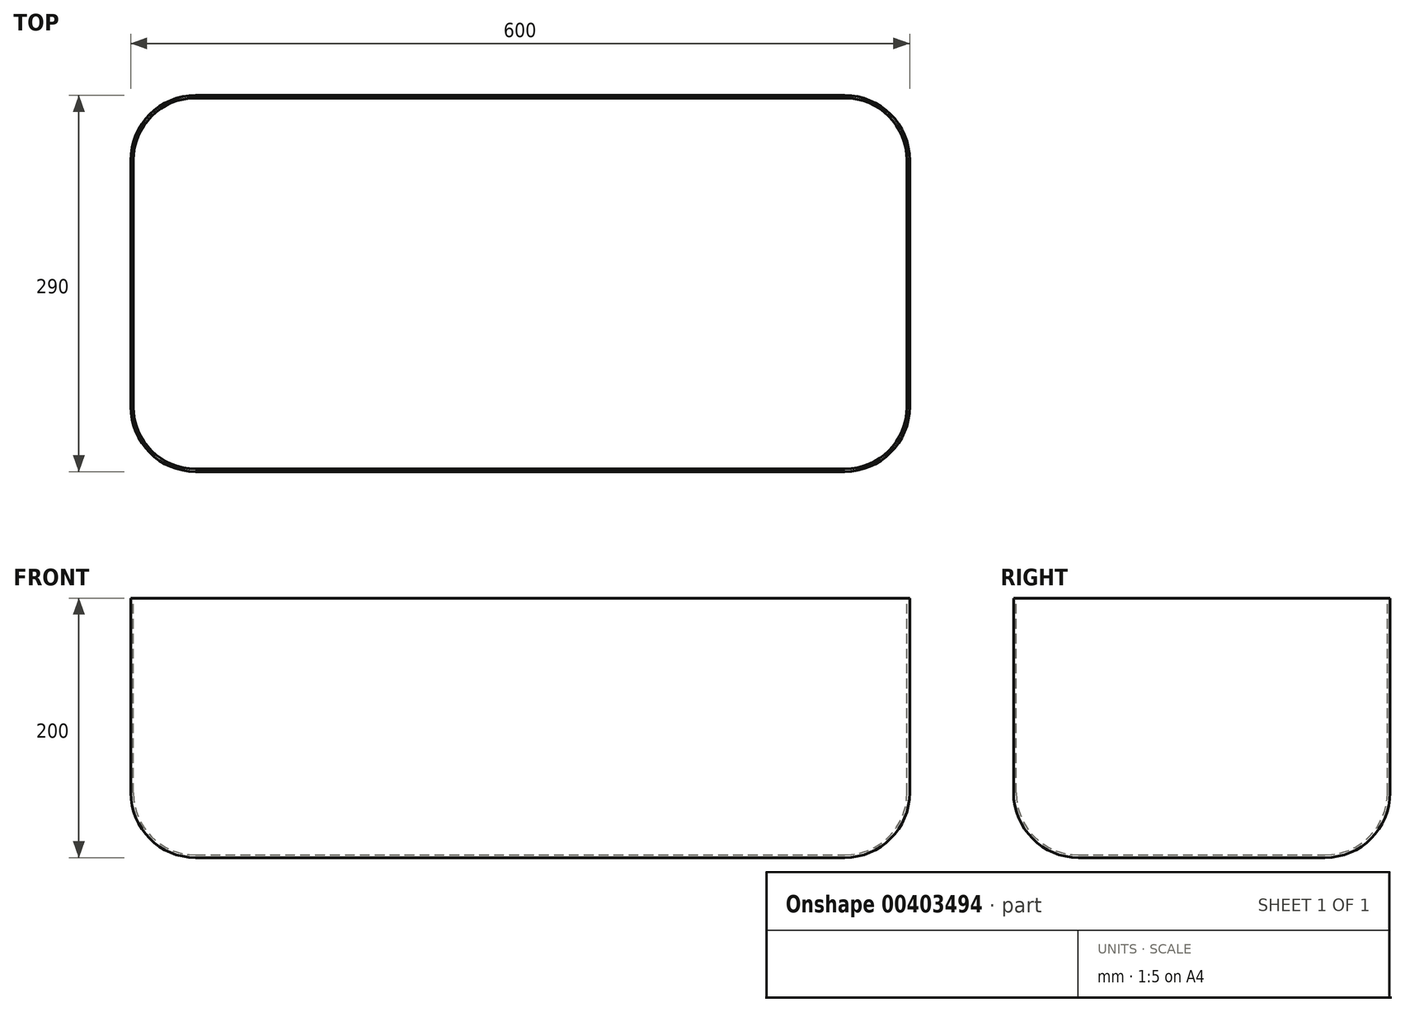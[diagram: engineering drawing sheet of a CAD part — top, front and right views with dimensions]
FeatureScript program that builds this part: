
annotation { "Feature Type Name" : "Feature", "Feature Type Description" : "" }
export const myFeature = defineFeature(function(context is Context, id is Id, definition is map)
    precondition{}
    {
        {
            var Q0;
            Q0=qCreatedBy(makeId("Front.planeOp"),FACE);
            var sketch = newSketch(context, id + "F0", { "sketchPlane" : qUnion([Q0])});
            skLineSegment(sketch, "E0.bottom", {"start": v(0, 0) * mm, "end": v(600, 0) * mm});
            skLineSegment(sketch, "E0.top", {"start": v(0, 200) * mm, "end": v(600, 200) * mm});
            skLineSegment(sketch, "E0.left", {"start": v(0, 0) * mm, "end": v(0, 200) * mm});
            skLineSegment(sketch, "E0.right", {"start": v(600, 0) * mm, "end": v(600, 200) * mm});
            skSolve(sketch);
        }
        {
            var Q0;
            Q0=qSketchRegion(id+"F0",true);
            extrude(context, id + "F1", {"entities" : qUnion([Q0]), "depth" : 290 * mm});
        }
        {
            var Q0;
            Q0=makeQuery(id+"F1.opExtrude","CAP_EDGE",EDGE,{"disambiguationData":[OSD([sQuery(id+"F0.wireOp",EDGE,"E0.right")])],"isStart":false});
            var Q1;
            Q1=makeQuery(id+"F1.opExtrude","CAP_EDGE",EDGE,{"disambiguationData":[OSD([sQuery(id+"F0.wireOp",EDGE,"E0.left")])],"isStart":false});
            var Q2;
            Q2=makeQuery(id+"F1.opExtrude","CAP_EDGE",EDGE,{"disambiguationData":[OSD([sQuery(id+"F0.wireOp",EDGE,"E0.right")])],"isStart":true});
            var Q3;
            Q3=makeQuery(id+"F1.opExtrude","SWEPT_EDGE",EDGE,{"disambiguationData":[OSD([sQuery(id+"F0.wireOp",EDGE,"E0.bottom"),sQuery(id+"F0.wireOp",EDGE,"E0.right")])]});
            var Q4;
            Q4=makeQuery(id+"F1.opExtrude","CAP_EDGE",EDGE,{"disambiguationData":[OSD([sQuery(id+"F0.wireOp",EDGE,"E0.bottom")])],"isStart":false});
            var Q5;
            Q5=makeQuery(id+"F1.opExtrude","SWEPT_EDGE",EDGE,{"disambiguationData":[OSD([sQuery(id+"F0.wireOp",EDGE,"E0.bottom"),sQuery(id+"F0.wireOp",EDGE,"E0.left")])]});
            var Q6;
            Q6=makeQuery(id+"F1.opExtrude","CAP_EDGE",EDGE,{"disambiguationData":[OSD([sQuery(id+"F0.wireOp",EDGE,"E0.left")])],"isStart":true});
            var Q7;
            Q7=makeQuery(id+"F1.opExtrude","CAP_EDGE",EDGE,{"disambiguationData":[OSD([sQuery(id+"F0.wireOp",EDGE,"E0.bottom")])],"isStart":true});
            fillet(context, id + "F2", {"entities" : qUnion([Q0, Q1, Q2, Q3, Q4, Q5, Q6, Q7]), "radius" : 50 * mm, "tangentPropagation" : true, "allowEdgeOverflow" : false});
        }
        {
            var Q0;
            Q0=makeQuery(id+"F1.opExtrude","SWEPT_FACE",FACE,{"disambiguationData":[OSD([sQuery(id+"F0.wireOp",EDGE,"E0.top")])]});
            shell(context, id + "F3", {"entities" : qUnion([Q0]), "thickness" : 2 * mm});
        }
    });
